# Revit family: QF_BOURGEAT_Transtherm_Four_a_chariot_10GN1_1
name_source: partatom
category: Equipement spécialisé
revit_build: Autodesk Revit 2015 (Build: 20140606_1530(x64)
units: mm (PartAtom-declared; Revit-internal decimal feet)

## types (4) — shared parameters
Certification = NF alimentaire
Charge max = 40.00 kg
Consommation énergétique = 6.5Kwh/h
Débit Eau Adoucie = 0.0 L/s
Fabricant = BOURGEAT
Fréquence = 50 Hz
Hauteur hors tout = 1430 mm  [stored 4.6916 ft]
Indice de protection = IP25
Intensité nominale = 22 A
Longueur hors tout = 795 mm  [stored 2.60827 ft]
Nature isolant = Laine_de_roche(60mm)
Phase = 3
Poids net à vide = 80.00 kg
Profondeur hors tout = 720 mm  [stored 2.3622 ft]
Puissance électrique  = 8700 W
Remarques Plomberie = Débit=0.000083L/s
Spécification du Fabricant = TRANS'THERM
Tension = 400 V
URL catalogue = http://www.bourgeat.fr

## type names (no varying parameters)
- 891210
- 891210 + 897500
- 891910
- 891910 + 897500

note: column(s) folded — value = type name in every type: Modèle, Type_de_modele

note: [stored X ft] marks values corroborated as IEEE doubles in the binary element streams (Revit-internal decimal feet)
